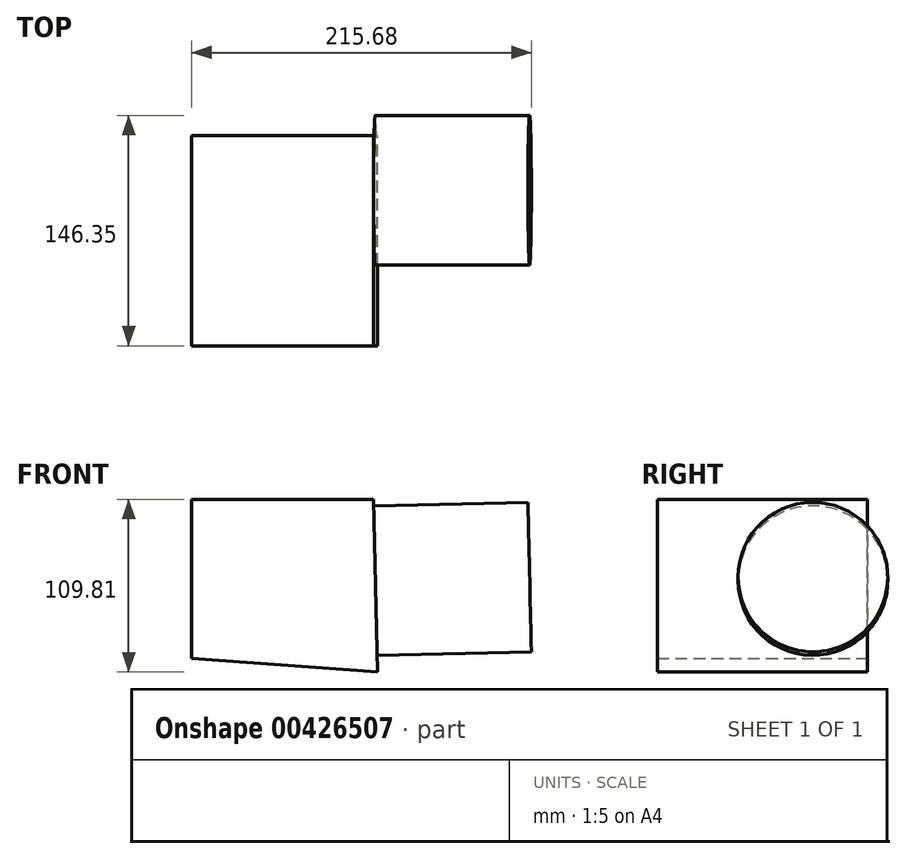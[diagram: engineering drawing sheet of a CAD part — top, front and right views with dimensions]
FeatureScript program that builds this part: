
annotation { "Feature Type Name" : "Feature", "Feature Type Description" : "" }
export const myFeature = defineFeature(function(context is Context, id is Id, definition is map)
    precondition{}
    {
        {
            var Q0;
            Q0=qCreatedBy(makeId("Front.planeOp"),FACE);
            var sketch = newSketch(context, id + "F0", { "sketchPlane" : qUnion([Q0])});
            skLineSegment(sketch, "E0", {"start": v(68.91, 53.26) * mm, "end": v(-46.46, 53.26) * mm});
            skLineSegment(sketch, "E1", {"start": v(-46.46, 53.26) * mm, "end": v(-46.46, -47.76) * mm});
            skLineSegment(sketch, "E2", {"start": v(-46.46, -47.76) * mm, "end": v(71.42, -56.55) * mm});
            skLineSegment(sketch, "E3", {"start": v(71.42, -56.55) * mm, "end": v(68.91, 53.26) * mm});
            skSolve(sketch);
        }
        {
            var Q0;
            Q0 = qSketchRegion(id + "F0", true);
            extrude(context, id + "F1", {"entities" : qUnion([Q0]), "depth" : 133.45 * mm});
        }
        {
            var Q0;
            Q0=makeQuery(id+"F1.opExtrude","SWEPT_FACE",FACE,{"disambiguationData":[OSD([sQuery(id+"F0.wireOp",EDGE,"E3")])]});
            var sketch = newSketch(context, id + "F2", { "sketchPlane" : qUnion([Q0])});
            skCircle(sketch, "E4", {"center": v(-34.6, 0) * mm, "radius": 47.5 * mm});
            skSolve(sketch);
        }
        {
            var Q0;
            Q0 = qSketchRegion(id + "F2", true);
            extrude(context, id + "F3", {"entities" : qUnion([Q0]), "operationType" : NewBodyOperationType.ADD, "depth" : 98.07 * mm});
        }
    });
